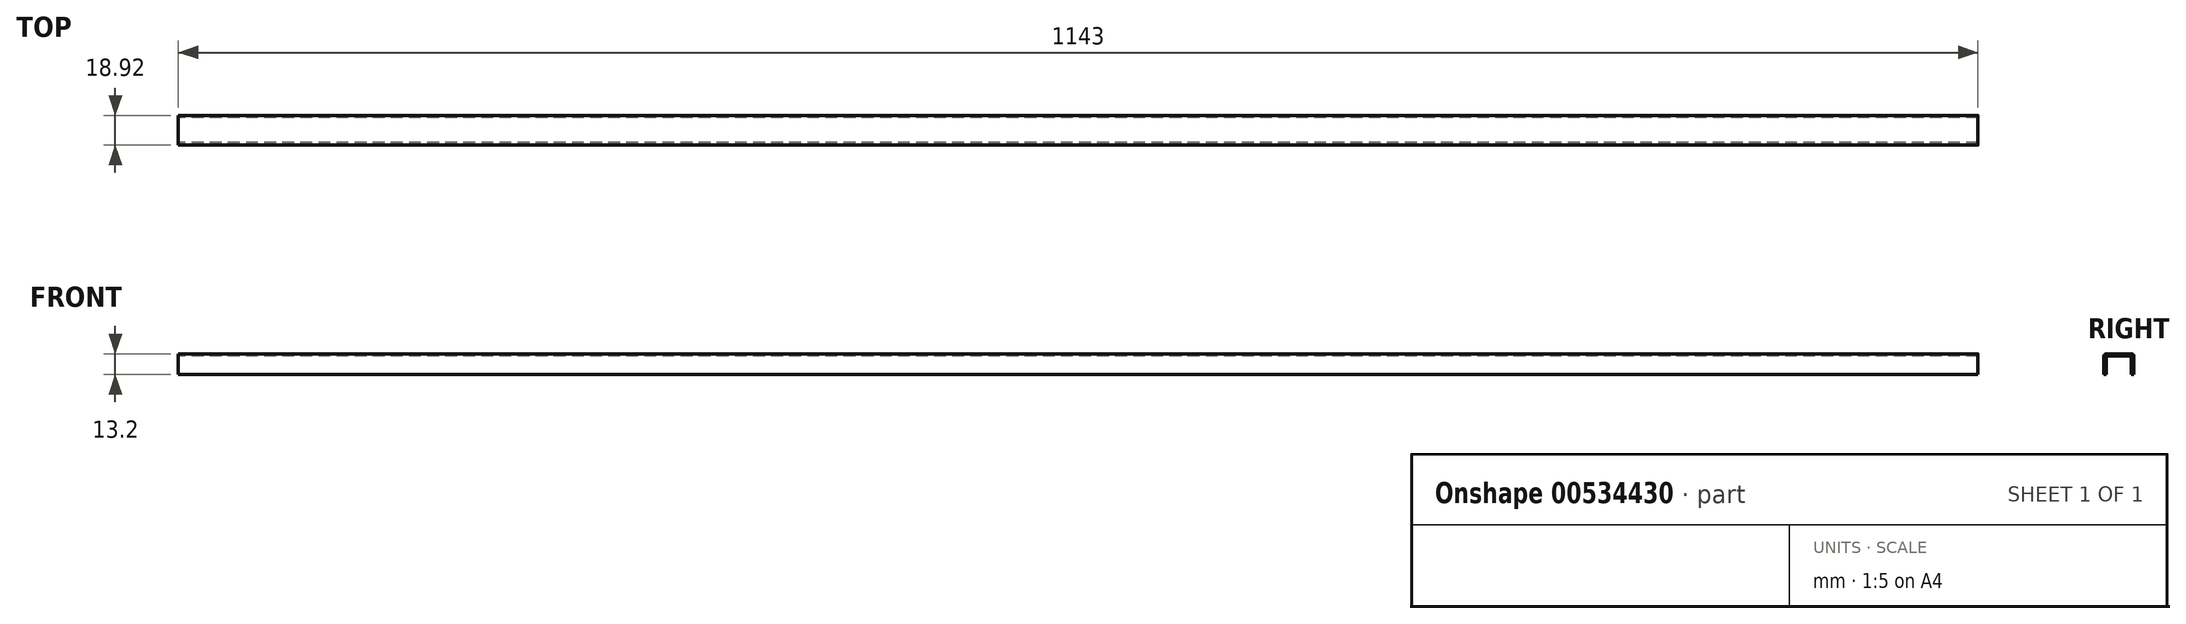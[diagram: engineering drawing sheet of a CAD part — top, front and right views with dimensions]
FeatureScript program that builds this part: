
annotation { "Feature Type Name" : "Feature", "Feature Type Description" : "" }
export const myFeature = defineFeature(function(context is Context, id is Id, definition is map)
    precondition{}
    {
        {
            var Q0;
            Q0=qCreatedBy(makeId("Right.planeOp"),FACE);
            var sketch = newSketch(context, id + "F0", { "sketchPlane" : qUnion([Q0])});
            skLineSegment(sketch, "E0", {"start": v(-9.46, 0) * mm, "end": v(-9.46, -11.68) * mm});
            skLineSegment(sketch, "E1", {"start": v(-9.46, -11.68) * mm, "end": v(-7.94, -11.68) * mm});
            skLineSegment(sketch, "E2", {"start": v(-7.94, -11.68) * mm, "end": v(-7.94, 0) * mm});
            skLineSegment(sketch, "E3", {"start": v(-7.94, 0) * mm, "end": v(7.94, 0) * mm});
            skLineSegment(sketch, "E4", {"start": v(7.94, 0) * mm, "end": v(7.94, -11.68) * mm});
            skLineSegment(sketch, "E5", {"start": v(7.94, -11.68) * mm, "end": v(9.46, -11.68) * mm});
            skLineSegment(sketch, "E6", {"start": v(9.46, -11.68) * mm, "end": v(9.46, 0) * mm});
            skLineSegment(sketch, "E7", {"start": v(7.94, 1.52) * mm, "end": v(-7.94, 1.52) * mm});
            skArc(sketch, "E8", {"start": v(-7.94, 1.52) * mm, "mid": v(-9.02, 1.08) * mm, "end": v(-9.46, 0) * mm});
            skArc(sketch, "E9", {"start": v(9.46, 0) * mm, "mid": v(9.02, 1.08) * mm, "end": v(7.94, 1.52) * mm});
            skSolve(sketch);
        }
        {
            var Q0;
            Q0=makeQuery(id+"F0.imprint","IMPRINT",FACE,{"disambiguationData":[TD([[makeQuery(id+"F0.imprint","IMPRINT",EDGE,{"derivedFrom":sQuery(id+"F0.wireOp",EDGE,"E0")}),1.0]])]});
            extrude(context, id + "F1", {"entities" : qUnion([Q0]), "endBound" : BoundingType.SYMMETRIC, "depth" : 2540 * mm, "offsetDistance" : 25.4 * mm});
        }
        {
            var Q0;
            Q0=qCreatedBy(makeId("Front.planeOp"),FACE);
            var sketch = newSketch(context, id + "F2", { "sketchPlane" : qUnion([Q0])});
            skLineSegment(sketch, "E10", {"start": v(-571.5, 1.52) * mm, "end": v(571.5, 1.52) * mm});
            skLineSegment(sketch, "E11", {"start": v(571.5, 1.52) * mm, "end": v(571.5, -11.68) * mm});
            skLineSegment(sketch, "E12", {"start": v(571.5, -11.68) * mm, "end": v(-571.5, -11.68) * mm});
            skLineSegment(sketch, "E13", {"start": v(-571.5, -11.68) * mm, "end": v(-571.5, 1.52) * mm});
            skSolve(sketch);
        }
        {
            var Q0;
            Q0=makeQuery(id+"F2.imprint","IMPRINT",FACE,{"disambiguationData":[TD([[makeQuery(id+"F2.imprint","IMPRINT",EDGE,{"derivedFrom":sQuery(id+"F2.wireOp",EDGE,"E10")}),-1.0]])]});
            extrude(context, id + "F3", {"entities" : qUnion([Q0]), "operationType" : NewBodyOperationType.INTERSECT, "endBound" : BoundingType.SYMMETRIC, "depth" : 2540 * mm, "offsetDistance" : 25.4 * mm});
        }
    });
